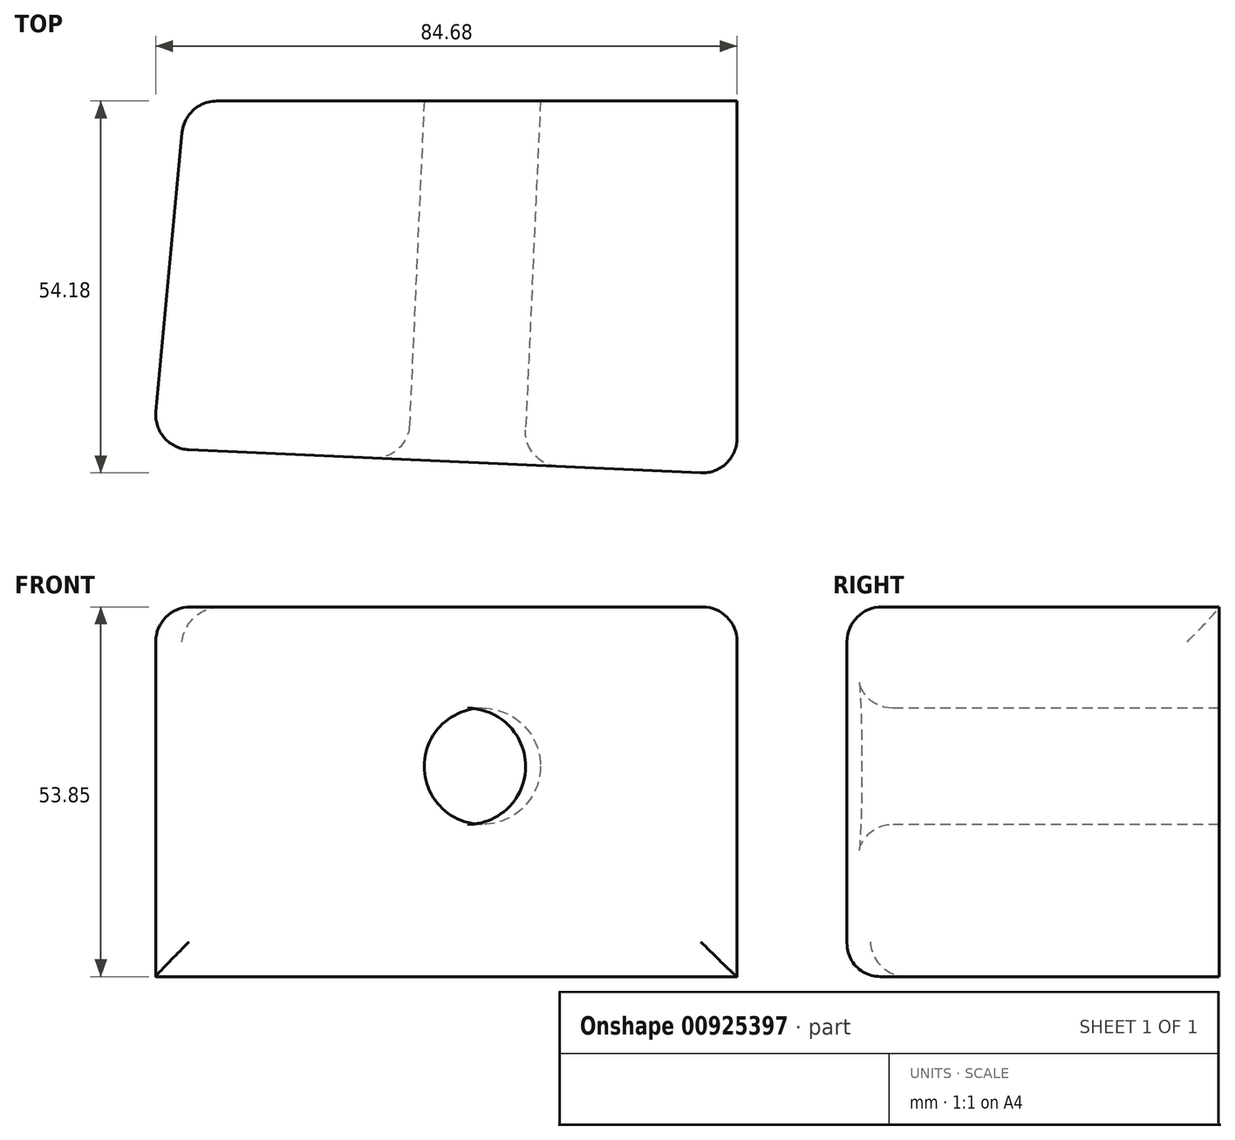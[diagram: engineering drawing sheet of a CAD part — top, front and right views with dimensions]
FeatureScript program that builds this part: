
annotation { "Feature Type Name" : "Feature", "Feature Type Description" : "" }
export const myFeature = defineFeature(function(context is Context, id is Id, definition is map)
    precondition{}
    {
        {
            var Q0;
            Q0=qCreatedBy(makeId("Top.planeOp"),FACE);
            var sketch = newSketch(context, id + "F0", { "sketchPlane" : qUnion([Q0])});
            skLineSegment(sketch, "E0", {"start": v(-55.66, 22.13) * mm, "end": v(24.75, 22.13) * mm});
            skLineSegment(sketch, "E1", {"start": v(24.75, 22.13) * mm, "end": v(24.75, -32.28) * mm});
            skLineSegment(sketch, "E2", {"start": v(24.75, -32.28) * mm, "end": v(-60.4, -28.43) * mm});
            skLineSegment(sketch, "E3", {"start": v(-60.4, -28.43) * mm, "end": v(-55.66, 22.13) * mm});
            skSolve(sketch);
        }
        {
            var Q0;
            Q0 = qSketchRegion(id + "F0", true);
            extrude(context, id + "F1", {"entities" : qUnion([Q0]), "depth" : 53.85 * mm, "offsetDistance" : 25.4 * mm});
        }
        {
            var Q0;
            Q0=makeQuery(id+"F1.opExtrude","SWEPT_FACE",FACE,{"disambiguationData":[OSD([sQuery(id+"F0.wireOp",EDGE,"E2")])]});
            var sketch = newSketch(context, id + "F2", { "sketchPlane" : qUnion([Q0])});
            skCircle(sketch, "E4", {"center": v(-13.35, 30.63) * mm, "radius": 8.46 * mm});
            skSolve(sketch);
        }
        {
            var Q0;
            Q0=makeQuery(id+"F2.imprint","IMPRINT",FACE,{"disambiguationData":[TD([[makeQuery(id+"F2.imprint","IMPRINT",EDGE,{"derivedFrom":sQuery(id+"F2.wireOp",EDGE,"E4")}),1.0]])]});
            extrude(context, id + "F3", {"entities" : qUnion([Q0]), "operationType" : NewBodyOperationType.REMOVE, "oppositeDirection" : true, "depth" : 64.26 * mm, "offsetDistance" : 25.4 * mm});
        }
        {
            var Q0;
            Q0=makeQuery(id+"F1.opExtrude","SWEPT_FACE",FACE,{"disambiguationData":[OSD([sQuery(id+"F0.wireOp",EDGE,"E2")])]});
            var Q1;
            Q1=makeQuery(id+"F1.opExtrude","CAP_EDGE",EDGE,{"disambiguationData":[OSD([sQuery(id+"F0.wireOp",EDGE,"E3")])],"isStart":false});
            var Q2;
            Q2=makeQuery(id+"F1.opExtrude","SWEPT_EDGE",EDGE,{"disambiguationData":[OSD([sQuery(id+"F0.wireOp",EDGE,"E0"),sQuery(id+"F0.wireOp",EDGE,"E3")])]});
            var Q3;
            Q3=makeQuery(id+"F1.opExtrude","CAP_EDGE",EDGE,{"disambiguationData":[OSD([sQuery(id+"F0.wireOp",EDGE,"E1")])],"isStart":false});
            fillet(context, id + "F4", {"entities" : qUnion([Q0, Q1, Q2, Q3]), "radius" : 5.08 * mm, "tangentPropagation" : true, "allowEdgeOverflow" : false});
        }
    });
